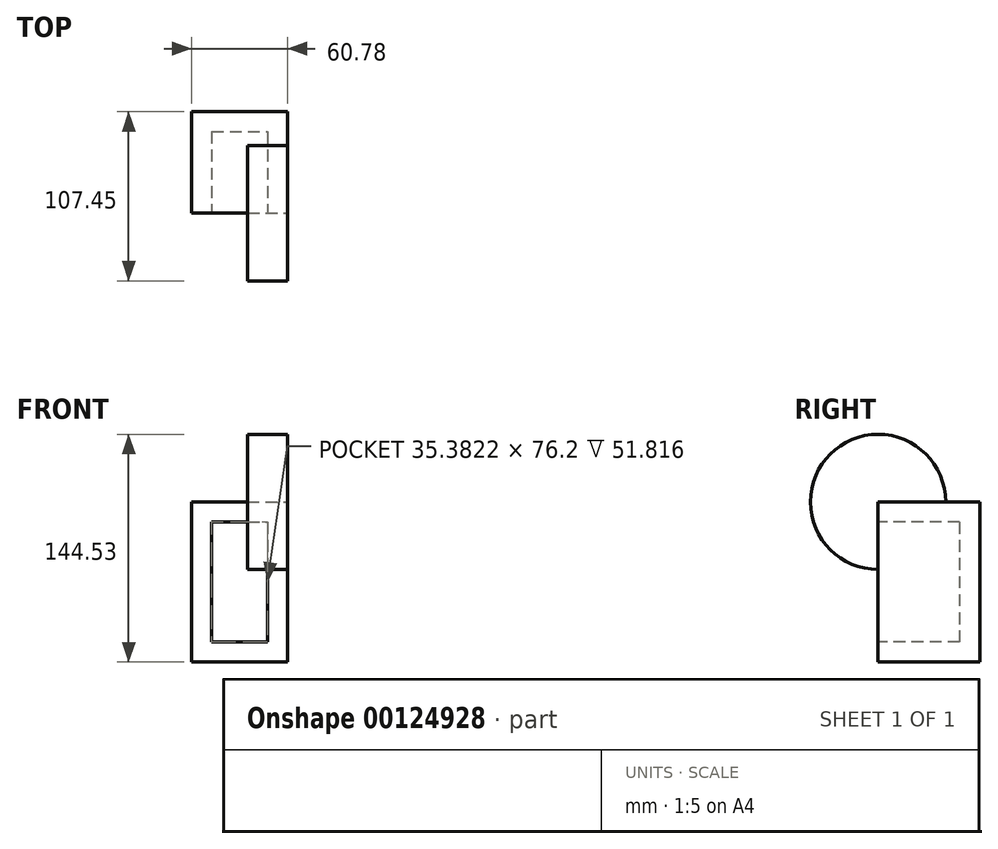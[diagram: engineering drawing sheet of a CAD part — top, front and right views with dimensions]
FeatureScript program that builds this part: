
annotation { "Feature Type Name" : "Feature", "Feature Type Description" : "" }
export const myFeature = defineFeature(function(context is Context, id is Id, definition is map)
    precondition{}
    {
        {
            var Q0;
            Q0=qCreatedBy(makeId("Top.planeOp"),FACE);
            var sketch = newSketch(context, id + "F0", { "sketchPlane" : qUnion([Q0])});
            skLineSegment(sketch, "E0.bottom", {"start": v(-30.4, 32.26) * mm, "end": v(30.4, 32.26) * mm});
            skLineSegment(sketch, "E0.top", {"start": v(-30.4, -32.26) * mm, "end": v(30.4, -32.26) * mm});
            skLineSegment(sketch, "E0.left", {"start": v(-30.4, 32.26) * mm, "end": v(-30.4, -32.26) * mm});
            skLineSegment(sketch, "E0.right", {"start": v(30.4, 32.26) * mm, "end": v(30.4, -32.26) * mm});
            skPoint(sketch, "E0.middle", {"position": v(0, 0) * mm});
            skSolve(sketch);
        }
        {
            var Q0;
            Q0=makeQuery(id+"F0.imprint","IMPRINT",FACE,{"disambiguationData":[TD([[makeQuery(id+"F0.imprint","IMPRINT",EDGE,{"derivedFrom":sQuery(id+"F0.wireOp",EDGE,"E0.bottom")}),-1.0]])]});
            extrude(context, id + "F1", {"entities" : qUnion([Q0]), "depth" : 101.6 * mm});
        }
        {
            var Q0;
            Q0=makeQuery(id+"F1.opExtrude","SWEPT_FACE",FACE,{"disambiguationData":[OSD([sQuery(id+"F0.wireOp",EDGE,"E0.top")])]});
            shell(context, id + "F2", {"entities" : qUnion([Q0]), "thickness" : 12.7 * mm});
        }
        {
            var Q0;
            Q0=makeQuery(id+"F1.opExtrude","SWEPT_FACE",FACE,{"disambiguationData":[OSD([sQuery(id+"F0.wireOp",EDGE,"E0.right")])]});
            var sketch = newSketch(context, id + "F3", { "sketchPlane" : qUnion([Q0])});
            skCircle(sketch, "E1", {"center": v(-32.26, 101.6) * mm, "radius": 42.93 * mm});
            skSolve(sketch);
        }
        {
            var Q0;
            {var subQ0=sQuery(id+"F3.wireOp",EDGE,"E1");var subQ1=sQuery(id+"F0.wireOp",EDGE,"E0.right");var subQ4=makeQuery(id+"F1.opExtrude","CAP_EDGE",EDGE,{"disambiguationData":[OSD([subQ1])],"isStart":false});var subQ5=makeQuery(id+"F3.imprint","INTERSECT",VERTEX,{"derivedFrom":[subQ4,subQ0]});Q0=makeQuery(id+"F3.imprint","IMPRINT",FACE,{"disambiguationData":[TD([[makeQuery(id+"F3.imprint","IMPRINT",EDGE,{"disambiguationData":[TD([[subQ5,-1.0]])],"derivedFrom":subQ0}),1.0]])]});}
            var Q1;
            Q1=makeQuery(id+"F1.opExtrude","SWEPT_FACE",FACE,{"disambiguationData":[OSD([sQuery(id+"F0.wireOp",EDGE,"E0.left")])]});
            extrude(context, id + "F4", {"entities" : qUnion([Q0]), "oppositeDirection" : true, "endBoundEntityFace" : qUnion([Q1]), "depth" : 25.4 * mm});
        }
    });
